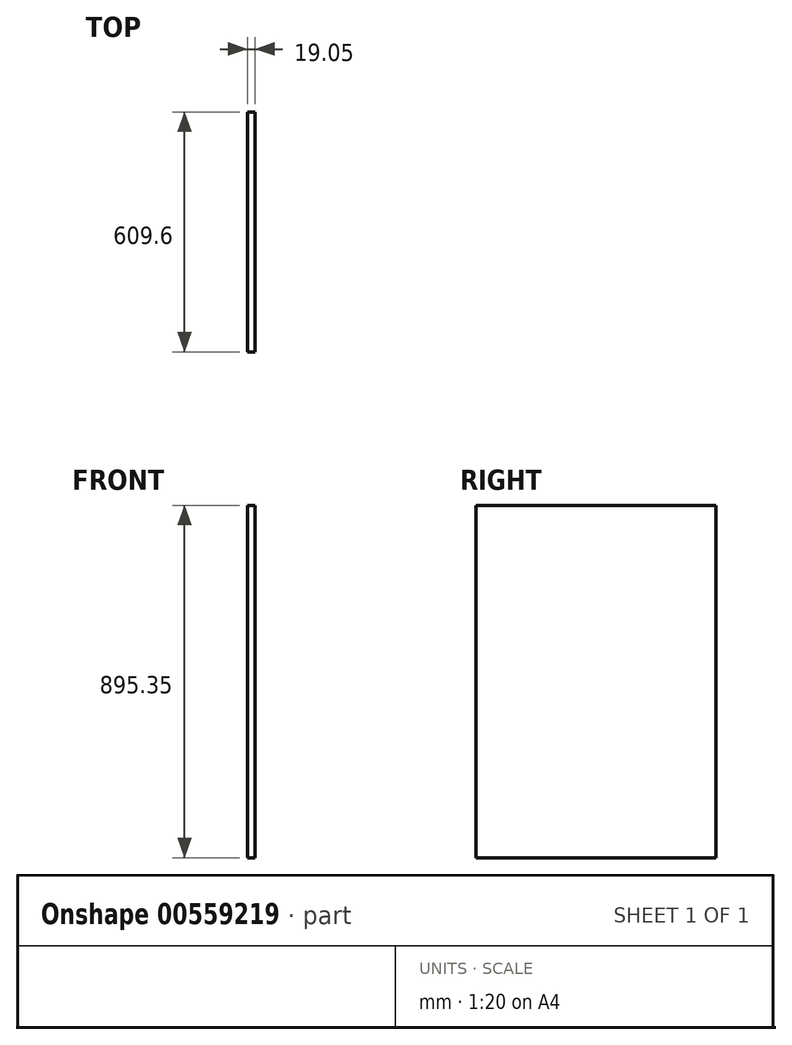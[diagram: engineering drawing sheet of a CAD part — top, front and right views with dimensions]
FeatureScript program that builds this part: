
annotation { "Feature Type Name" : "Feature", "Feature Type Description" : "" }
export const myFeature = defineFeature(function(context is Context, id is Id, definition is map)
    precondition{}
    {
        {
            var Q0;
            Q0=qCreatedBy(makeId("Right.planeOp"),FACE);
            var sketch = newSketch(context, id + "F0", { "sketchPlane" : qUnion([Q0])});
            skLineSegment(sketch, "E0.bottom", {"start": v(0, 0) * mm, "end": v(609.6, 0) * mm});
            skLineSegment(sketch, "E0.top", {"start": v(0, 895.35) * mm, "end": v(609.6, 895.35) * mm});
            skLineSegment(sketch, "E0.left", {"start": v(0, 0) * mm, "end": v(0, 895.35) * mm});
            skLineSegment(sketch, "E0.right", {"start": v(609.6, 0) * mm, "end": v(609.6, 895.35) * mm});
            skSolve(sketch);
        }
        {
            var Q0;
            Q0=makeQuery(id+"F0.imprint","IMPRINT",FACE,{"disambiguationData":[TD([[makeQuery(id+"F0.imprint","IMPRINT",EDGE,{"derivedFrom":sQuery(id+"F0.wireOp",EDGE,"E0.bottom")}),1.0]])]});
            extrude(context, id + "F1", {"entities" : qUnion([Q0]), "depth" : 19.05 * mm, "offsetDistance" : 25.4 * mm});
        }
    });
